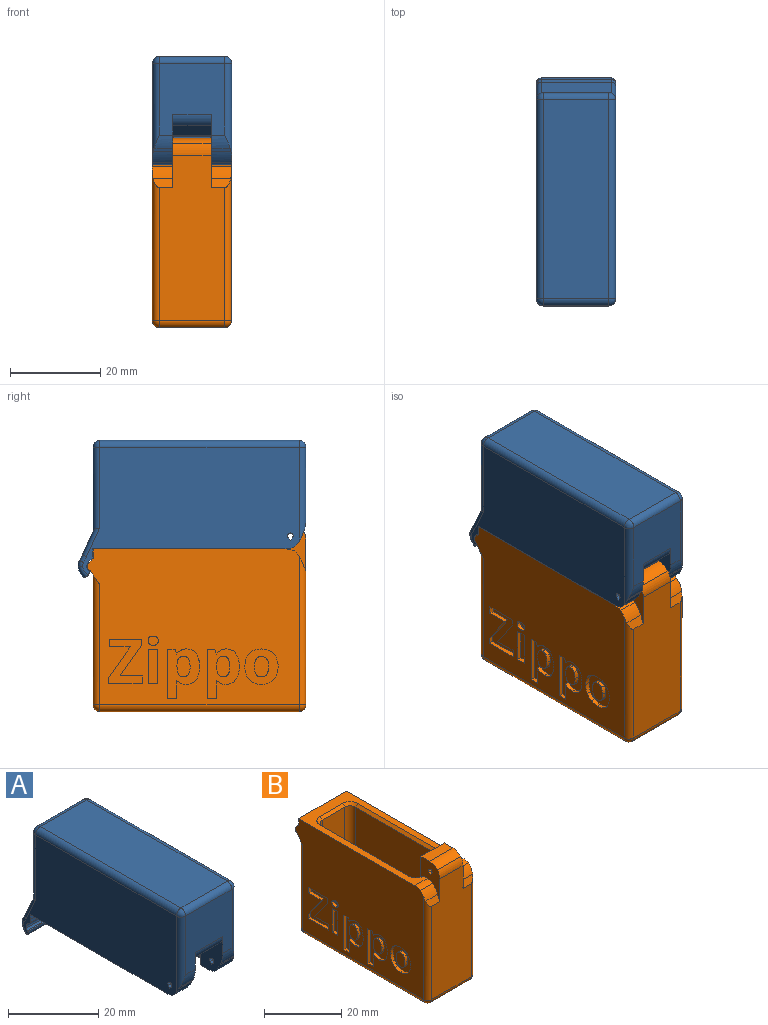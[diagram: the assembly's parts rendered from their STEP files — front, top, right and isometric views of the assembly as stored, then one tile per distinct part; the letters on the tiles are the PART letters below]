
ASSEMBLY  parts=2 mates=1
PART A: 71 faces, bbox 17.6x50.8x31 mm
  f0: plane 18.7x14.5mm, normal (0,1,0), area 271.2mm2, adj f27,f44,f45,f61
  f1: plane 15.91x14.5mm, normal (0,-1,0), area 191.4mm2, adj f15,f16,f50,f51,f54,f57,f58,f64
  f2: cylinder r=2mm len=21mm, axis (0,0,-1), area 64.4mm2, adj f3,f7,f12,f13,f15,f67
  f3: plane 13.1x8.2mm, normal (0,1,0), area 107.4mm2, adj f2,f4,f13,f66
  f4: cylinder r=2mm len=21mm, axis (0,0,-1), area 64.4mm2, adj f3,f8,f12,f13,f16,f65
  f5: plane 47.92x28.3mm, normal (-1,0,0), area 1000.2mm2, adj f12,f17,f18,f19,f24,f28,f29,f30
  f6: cylinder r=2mm len=21mm, axis (0,0,-1), area 66mm2, adj f7,f10,f12,f13
  f7: plane 32.2x21mm, normal (-1,0,0), area 676.2mm2, adj f2,f6,f12,f13
  f8: plane 32.2x21mm, normal (1,0,0), area 676.2mm2, adj f4,f9,f12,f13
  f9: cylinder r=2mm len=21mm, axis (0,0,-1), area 66mm2, adj f8,f10,f12,f13
  f10: plane 21x8.2mm, normal (0,-1,0), area 172.2mm2, adj f6,f9,f12,f13
  f11: plane 47.92x28.3mm, normal (1,0,0), area 1000.2mm2, adj f12,f20,f21,f22,f24,f28,f29,f30
  f12: plane 42.56x17.5mm, normal (0,0,-1), area 287.2mm2, adj f2,f4,f5,f6,f7,f8,f9,f10
  f13: plane 36.2x12.2mm, normal (0,0,-1), area 438.2mm2, adj f2,f3,f4,f6,f7,f8,f9,f10
  f14: plane 44.1x14.5mm, normal (0,0,1), area 639.4mm2, adj f56,f58,f61,f62
  f15: plane 11.19x6.94mm, normal (-1,0,0), area 45.1mm2, adj f1,f2,f12,f20,f21,f22,f23,f46
  f16: plane 11.19x6.94mm, normal (1,0,0), area 45.1mm2, adj f1,f4,f12,f17,f18,f19,f23,f47
  f17: plane 4.45x0.61mm, normal (0,0.79,0.61), area 3.4mm2, adj f5,f16,f18,f19
  f18: plane 4.45x0.61mm, normal (0,-0.79,0.61), area 3.4mm2, adj f5,f16,f17,f19
  f19: cylinder r=0.62mm len=4.45mm, axis (-1,0,0), area 12.7mm2, adj f5,f16,f17,f18
  f20: cylinder r=0.62mm len=4.45mm, axis (-1,0,0), area 12.7mm2, adj f11,f15,f21,f22
  f21: plane 4.45x0.61mm, normal (0,-0.79,0.61), area 3.4mm2, adj f11,f15,f20,f22
  f22: plane 4.45x0.61mm, normal (0,0.79,0.61), area 3.4mm2, adj f11,f15,f20,f21
  f23: plane 8.6x3.23mm, normal (0,-0.57,-0.82), area 33.9mm2, adj f15,f16,f64,f68,f69,f70
  f24: cylinder r=1.26mm len=17.5mm, axis (1,0,0), area 36.3mm2, adj f5,f11,f25,f34,f36,f40
  f25: cylinder r=3.7mm len=15.5mm, axis (1,0,0), area 43.2mm2, adj f24,f26,f36,f40
  f26: cylinder r=2.41mm len=15.5mm, axis (1,0,0), area 21.6mm2, adj f25,f35,f37,f41
  f27: plane 15.59x5.41mm, normal (0,0.91,0.42), area 87.7mm2, adj f0,f35,f39,f43,f44,f45
  f28: plane 17.5x1.21mm, normal (0,-1,0), area 21.2mm2, adj f5,f11,f12,f29
  f29: plane 17.5x0.87mm, normal (0,-1,0), area 15.1mm2, adj f5,f11,f28,f30
  f30: plane 17.5x0.36mm, normal (0,-0.69,-0.72), area 8.6mm2, adj f5,f11,f29,f31
  f31: cylinder r=4.29mm len=17.5mm, axis (1,0,0), area 17.6mm2, adj f5,f11,f30,f32
  f32: cylinder r=1.22mm len=17.5mm, axis (1,0,0), area 19.9mm2, adj f5,f11,f31,f33
  f33: cylinder r=1.4mm len=17.5mm, axis (1,0,0), area 11.3mm2, adj f5,f11,f32,f34
  f34: cylinder r=1.26mm len=17.5mm, axis (1,0,0), area 3.8mm2, adj f5,f11,f24,f33
  f35: cylinder r=15mm len=15.5mm, axis (1,0,0), area 21.5mm2, adj f26,f27,f38,f42
  f36: torus R=2.7mm, axis (1,0,0), area 4.3mm2, adj f11,f24,f25,f37
  f37: torus R=1.41mm, axis (1,0,0), area 1.9mm2, adj f11,f26,f36,f38
  f38: torus R=16mm, axis (1,0,0), area 2.2mm2, adj f11,f35,f37,f39
  f39: cylinder r=1mm len=6.84mm, axis (0,-0.42,0.91), area 10.1mm2, adj f11,f27,f38,f45
  f40: torus R=2.7mm, axis (1,0,0), area 4.3mm2, adj f5,f24,f25,f41
  f41: torus R=1.41mm, axis (1,0,0), area 1.9mm2, adj f5,f26,f40,f42
  f42: torus R=16mm, axis (1,0,0), area 2.2mm2, adj f5,f35,f41,f43
  f43: cylinder r=1mm len=6.84mm, axis (0,0.42,-0.91), area 10.1mm2, adj f5,f27,f42,f44
  f44: cylinder r=1.5mm len=18.7mm, axis (0,0,-1), area 43mm2, adj f0,f5,f27,f43,f59
  f45: cylinder r=1.5mm len=18.7mm, axis (0,0,1), area 43mm2, adj f0,f11,f27,f39,f63
  f46: plane 4.29x0.49mm, normal (0,-0.92,-0.38), area 2.2mm2, adj f15,f49,f50,f57
  f47: plane 4.29x0.49mm, normal (0,-0.92,-0.38), area 2.2mm2, adj f16,f48,f51,f54
  f48: cylinder r=8mm len=4.45mm, axis (1,0,0), area 13.9mm2, adj f5,f16,f47,f53,f54
  f49: cylinder r=8mm len=4.45mm, axis (1,0,0), area 13.9mm2, adj f11,f15,f46,f52,f57
  f50: cylinder r=8mm len=4.16mm, axis (-1,0,0), area 11.2mm2, adj f1,f15,f46,f57
  f51: cylinder r=8mm len=4.16mm, axis (-1,0,0), area 11.2mm2, adj f1,f16,f47,f54
  f52: cylinder r=5mm len=4.45mm, axis (1,0,0), area 9.6mm2, adj f11,f12,f15,f49
  f53: cylinder r=5mm len=4.45mm, axis (1,0,0), area 9.6mm2, adj f5,f12,f16,f48
  f54: cylinder r=1.5mm len=20.76mm, axis (0,0,1), area 43.4mm2, adj f1,f5,f47,f48,f51,f55
  f55: sphere r=1.5mm, area 3.5mm2, adj f54,f56,f58
  f56: cylinder r=1.5mm len=44.1mm, axis (0,1,0), area 103.9mm2, adj f5,f14,f55,f59
  f57: cylinder r=1.5mm len=20.76mm, axis (0,0,-1), area 43.4mm2, adj f1,f11,f46,f49,f50,f60
  f58: cylinder r=1.5mm len=14.5mm, axis (-1,0,0), area 34.2mm2, adj f1,f14,f55,f60
  f59: sphere r=1.5mm, area 4.8mm2, adj f44,f56,f61
  f60: sphere r=1.5mm, area 3.5mm2, adj f57,f58,f62
  f61: cylinder r=1.5mm len=14.5mm, axis (1,0,0), area 34.2mm2, adj f0,f14,f59,f63
  f62: cylinder r=1.5mm len=44.1mm, axis (0,-1,0), area 103.9mm2, adj f11,f14,f60,f63
  f63: sphere r=1.5mm, area 2.3mm2, adj f45,f61,f62
  f64: cylinder r=3mm len=8.6mm, axis (-1,0,0), area 24.8mm2, adj f1,f15,f16,f23
  f65: cone r=2mm half-angle=45deg, axis (0,0,-1), area 0.4mm2, adj f4,f16,f66,f70
  f66: plane 8.2x1.37mm, normal (0,0.71,-0.71), area 15.9mm2, adj f3,f65,f67,f69
  f67: cone r=2mm half-angle=45deg, axis (0,0,-1), area 0.4mm2, adj f2,f15,f66,f68
  f68: bspline ~1.03x0.24mm, area 0.2mm2, adj f15,f23,f67,f69
  f69: cylinder r=0.8mm len=8.2mm, axis (1,0,0), area 9.2mm2, adj f23,f66,f68,f70
  f70: bspline ~1.03x0.24mm, area 0.2mm2, adj f16,f23,f65,f69
PART B: 227 faces, bbox 17.5x48.4x41.9 mm
  f0: plane 44.1x14.5mm, normal (0,0,-1), area 594.4mm2, adj f125,f126,f127,f128,f129,f130,f131,f132
  f1: plane 46.9x34.5mm, normal (-1,0,0), area 1314.9mm2, adj f13,f14,f22,f23,f24,f25,f33,f34
  f2: plane 28.73x14.5mm, normal (0,1,0), area 416.5mm2, adj f25,f213,f214,f222
  f3: plane 36.65x14.5mm, normal (0,-1,0), area 488.5mm2, adj f16,f17,f207,f208,f211,f212,f218,f223
  f4: plane 46.9x34.5mm, normal (1,0,0), area 1533.1mm2, adj f13,f14,f22,f23,f24,f25,f210,f212
  f5: cylinder r=2mm len=32.2mm, axis (0,0,-1), area 101.2mm2, adj f6,f12,f15,f202
  f6: plane 32.2x32.2mm, normal (-1,0,0), area 1036.8mm2, adj f5,f7,f15,f201
  f7: cylinder r=2mm len=32.2mm, axis (0,0,-1), area 101.2mm2, adj f6,f8,f15,f200
  f8: plane 38.9x8.5mm, normal (0,1,0), area 321mm2, adj f7,f9,f15,f16,f17,f18,f200,f206
  f9: cylinder r=2mm len=32.2mm, axis (0,0,-1), area 101.2mm2, adj f8,f10,f15,f206
  f10: plane 32.2x32.2mm, normal (1,0,0), area 1036.8mm2, adj f9,f11,f15,f205
  f11: cylinder r=2mm len=32.2mm, axis (0,0,-1), area 101.2mm2, adj f10,f12,f15,f204
  f12: plane 32.2x8.2mm, normal (0,-1,0), area 264mm2, adj f5,f11,f15,f203
  f13: plane 17.5x2.1mm, normal (0,1,0), area 36.8mm2, adj f1,f4,f14,f22
  f14: plane 42.46x17.5mm, normal (0,0,1), area 215.8mm2, adj f1,f4,f13,f16,f17,f200,f201,f202
  f15: plane 36.2x12.2mm, normal (0,0,1), area 438.2mm2, adj f5,f6,f7,f8,f9,f10,f11,f12
  f16: plane 10.91x6.91mm, normal (-1,0,0), area 43.2mm2, adj f3,f8,f14,f18,f19,f20,f21,f206
  f17: plane 10.91x6.91mm, normal (1,0,0), area 43.2mm2, adj f3,f8,f14,f18,f19,f20,f21,f200
  f18: plane 8.5x3.16mm, normal (0,0,1), area 26.9mm2, adj f8,f16,f17,f217
  f19: cylinder r=0.62mm len=8.5mm, axis (-1,0,0), area 24.3mm2, adj f16,f17,f20,f21
  f20: plane 8.5x0.61mm, normal (0,-0.79,0.61), area 6.6mm2, adj f16,f17,f19,f21
  f21: plane 8.5x0.61mm, normal (0,0.79,0.61), area 6.6mm2, adj f16,f17,f19,f20
  f22: plane 17.5x0.81mm, normal (0,0.71,0.71), area 20.2mm2, adj f1,f4,f13,f23
  f23: cylinder r=2mm len=17.5mm, axis (-1,0,0), area 12mm2, adj f1,f4,f22,f24
  f24: cylinder r=1mm len=17.5mm, axis (-1,0,0), area 29mm2, adj f1,f4,f23,f25
  f25: plane 17.5x3.09mm, normal (0,0.82,-0.57), area 21.7mm2, adj f1,f2,f4,f24,f213,f214
  f26: extruded ~1.12x1mm, area 1.3mm2, adj f27,f48,f49,f116
  f27: extruded ~1.07x1mm, area 1.3mm2, adj f26,f28,f49,f116
  f28: extruded ~1.68x1mm, area 1.7mm2, adj f27,f29,f49,f116
  f29: extruded ~2.29x1.39mm, area 3mm2, adj f28,f30,f49,f116
  f30: extruded ~1.15x1mm, area 1.3mm2, adj f29,f31,f49,f116
  f31: extruded ~1.75x1mm, area 1.8mm2, adj f30,f32,f49,f116
  f32: plane 1x0.23mm, normal (0,1,0), area 0.2mm2, adj f31,f48,f49,f116
  f33: extruded ~2.09x1mm, area 2.4mm2, adj f1,f34,f47,f49
  f34: extruded ~1.54x1mm, area 1.6mm2, adj f1,f33,f35,f49
  f35: extruded ~1.36x1.01mm, area 1.7mm2, adj f1,f34,f36,f49
  f36: extruded ~2.11x1mm, area 2.1mm2, adj f1,f35,f37,f49
  f37: extruded ~2.88x1mm, area 3mm2, adj f1,f36,f38,f49
  f38: extruded ~2.1x1.04mm, area 2.4mm2, adj f1,f37,f39,f49
  f39: extruded ~2.15x1.12mm, area 2.5mm2, adj f1,f38,f40,f49
  f40: plane 1x0.1mm, normal (0,0,-1), area 0.1mm2, adj f1,f39,f41,f49
  f41: plane 1x0.98mm, normal (0,0.96,-0.28), area 1mm2, adj f1,f40,f42,f49
  f42: plane 1.68x1mm, normal (0,0,-1), area 1.7mm2, adj f1,f41,f43,f49
  f43: plane 10.91x1mm, normal (0,-1,0), area 10.9mm2, adj f1,f42,f44,f49
  f44: plane 2.07x1mm, normal (0,0,1), area 2.1mm2, adj f1,f43,f45,f49
  f45: plane 3.07x1mm, normal (0,1,0), area 3.1mm2, adj f1,f44,f46,f49
  f46: extruded ~1.1x1mm, area 1.1mm2, adj f1,f45,f47,f49
  f47: plane 1x0.11mm, normal (0,0,1), area 0.1mm2, adj f1,f33,f46,f49
  f48: extruded ~1.55x1mm, area 1.6mm2, adj f26,f32,f49,f116
  f49: plane 11.05x7.07mm, normal (-1,0,0), area 45.1mm2, adj f26,f27,f28,f29,f30,f31,f32,f33
  f50: extruded ~1.12x1mm, area 1.3mm2, adj f51,f72,f73,f117
  f51: extruded ~1.07x1mm, area 1.3mm2, adj f50,f52,f73,f117
  f52: extruded ~1.68x1mm, area 1.7mm2, adj f51,f53,f73,f117
  f53: extruded ~2.29x1.39mm, area 3mm2, adj f52,f54,f73,f117
  f54: extruded ~1.15x1mm, area 1.3mm2, adj f53,f55,f73,f117
  f55: extruded ~1.75x1mm, area 1.8mm2, adj f54,f56,f73,f117
  f56: plane 1x0.23mm, normal (0,1,0), area 0.2mm2, adj f55,f72,f73,f117
  f57: extruded ~2.09x1mm, area 2.4mm2, adj f1,f58,f71,f73
  f58: extruded ~1.54x1mm, area 1.6mm2, adj f1,f57,f59,f73
  f59: extruded ~1.36x1.01mm, area 1.7mm2, adj f1,f58,f60,f73
  f60: extruded ~2.11x1mm, area 2.1mm2, adj f1,f59,f61,f73
  f61: extruded ~2.88x1mm, area 3mm2, adj f1,f60,f62,f73
  f62: extruded ~2.1x1.04mm, area 2.4mm2, adj f1,f61,f63,f73
  f63: extruded ~2.15x1.12mm, area 2.5mm2, adj f1,f62,f64,f73
  f64: plane 1x0.1mm, normal (0,0,-1), area 0.1mm2, adj f1,f63,f65,f73
  f65: plane 1x0.98mm, normal (0,0.96,-0.28), area 1mm2, adj f1,f64,f66,f73
  f66: plane 1.68x1mm, normal (0,0,-1), area 1.7mm2, adj f1,f65,f67,f73
  f67: plane 10.91x1mm, normal (0,-1,0), area 10.9mm2, adj f1,f66,f68,f73
  f68: plane 2.07x1mm, normal (0,0,1), area 2.1mm2, adj f1,f67,f69,f73
  f69: plane 3.07x1mm, normal (0,1,0), area 3.1mm2, adj f1,f68,f70,f73
  f70: extruded ~1.1x1mm, area 1.1mm2, adj f1,f69,f71,f73
  f71: plane 1x0.11mm, normal (0,0,1), area 0.1mm2, adj f1,f57,f70,f73
  f72: extruded ~1.55x1mm, area 1.6mm2, adj f50,f56,f73,f117
  f73: plane 11.05x7.07mm, normal (-1,0,0), area 45.1mm2, adj f50,f51,f52,f53,f54,f55,f56,f57
  f74: extruded ~2.89x1mm, area 3.1mm2, adj f1,f75,f91,f92
  f75: extruded ~2.08x1mm, area 2.1mm2, adj f1,f74,f76,f92
  f76: extruded ~1.36x1.28mm, area 1.9mm2, adj f1,f75,f77,f92
  f77: extruded ~1.92x1mm, area 2mm2, adj f1,f76,f78,f92
  f78: extruded ~2.72x1.03mm, area 3mm2, adj f1,f77,f79,f92
  f79: extruded ~2.89x1mm, area 3.1mm2, adj f1,f78,f80,f92
  f80: extruded ~2.09x1mm, area 2.2mm2, adj f1,f79,f81,f92
  f81: extruded ~1.37x1.28mm, area 1.9mm2, adj f1,f80,f82,f92
  f82: extruded ~1.92x1mm, area 2mm2, adj f1,f81,f91,f92
  f83: extruded ~1.7x1mm, area 1.8mm2, adj f84,f90,f92,f93
  f84: extruded ~1.69x1mm, area 1.8mm2, adj f83,f85,f92,f93
  f85: extruded ~1.19x1mm, area 1.4mm2, adj f84,f86,f92,f93
  f86: extruded ~1.2x1mm, area 1.4mm2, adj f85,f87,f92,f93
  f87: extruded ~1.69x1mm, area 1.7mm2, adj f86,f88,f92,f93
  f88: extruded ~1.7x1mm, area 1.8mm2, adj f87,f89,f92,f93
  f89: extruded ~1.19x1mm, area 1.4mm2, adj f88,f90,f92,f93
  f90: extruded ~1.2x1mm, area 1.4mm2, adj f83,f89,f92,f93
  f91: extruded ~2.72x1.04mm, area 3mm2, adj f1,f74,f82,f92
  f92: plane 7.85x7.34mm, normal (-1,0,0), area 35.1mm2, adj f74,f75,f76,f77,f78,f79,f80,f81
  f93: plane 4.53x3.12mm, normal (-1,0,0), area 11.9mm2, adj f83,f84,f85,f86,f87,f88,f89,f90
  f94: plane 2.07x1mm, normal (0,0,1), area 2.1mm2, adj f1,f95,f97,f98
  f95: plane 7.58x1mm, normal (0,1,0), area 7.6mm2, adj f1,f94,f96,f98
  f96: plane 2.07x1mm, normal (0,0,-1), area 2.1mm2, adj f1,f95,f97,f98
  f97: plane 7.58x1mm, normal (0,-1,0), area 7.6mm2, adj f1,f94,f96,f98
  f98: plane 7.58x2.07mm, normal (-1,0,0), area 15.7mm2, adj f94,f95,f96,f97
  f99: extruded ~1.13x1.01mm, area 1.7mm2, adj f1,f100,f103,f104
  f100: extruded ~1.13x1.02mm, area 1.7mm2, adj f1,f99,f101,f104
  f101: extruded ~1x0.84mm, area 0.9mm2, adj f1,f100,f102,f104
  f102: extruded ~1x0.75mm, area 0.8mm2, adj f1,f101,f103,f104
  f103: extruded ~1.13x1.01mm, area 1.7mm2, adj f1,f99,f102,f104
  f104: plane 2.25x2.03mm, normal (-1,0,0), area 3.8mm2, adj f99,f100,f101,f102,f103
  f105: plane 7.37x1mm, normal (0,0,1), area 7.4mm2, adj f1,f106,f114,f115
  f106: plane 1.73x1mm, normal (0,1,0), area 1.7mm2, adj f1,f105,f107,f115
  f107: plane 4.87x1mm, normal (0,0,-1), area 4.9mm2, adj f1,f106,f108,f115
  f108: plane 6.82x4.74mm, normal (0,0.82,0.57), area 8.3mm2, adj f1,f107,f109,f115
  f109: plane 1.36x1mm, normal (0,1,0), area 1.4mm2, adj f1,f108,f110,f115
  f110: plane 7.11x1mm, normal (0,0,-1), area 7.1mm2, adj f1,f109,f111,f115
  f111: plane 1.73x1mm, normal (0,-1,0), area 1.7mm2, adj f1,f110,f112,f115
  f112: plane 4.62x1mm, normal (0,0,1), area 4.6mm2, adj f1,f111,f113,f115
  f113: plane 6.81x4.75mm, normal (0,-0.82,-0.57), area 8.3mm2, adj f1,f112,f114,f115
  f114: plane 1.36x1mm, normal (0,-1,0), area 1.4mm2, adj f1,f105,f113,f115
  f115: plane 9.91x7.37mm, normal (-1,0,0), area 39.4mm2, adj f105,f106,f107,f108,f109,f110,f111,f112
  f116: plane 4.53x2.9mm, normal (-1,0,0), area 11.1mm2, adj f26,f27,f28,f29,f30,f31,f32,f48
  f117: plane 4.53x2.9mm, normal (-1,0,0), area 11.1mm2, adj f50,f51,f52,f53,f54,f55,f56,f72
  f118: extruded ~0.52x0.4mm, area 0.2mm2, adj f119,f143,f144,f198
  f119: extruded ~0.56x0.4mm, area 0.3mm2, adj f118,f120,f144,f198
  f120: extruded ~0.7x0.4mm, area 0.3mm2, adj f119,f121,f144,f198
  f121: extruded ~0.49x0.4mm, area 0.2mm2, adj f120,f122,f144,f198
  f122: extruded ~0.56x0.4mm, area 0.2mm2, adj f121,f123,f144,f198
  f123: extruded ~0.52x0.4mm, area 0.2mm2, adj f122,f124,f144,f198
  f124: extruded ~0.59x0.4mm, area 0.2mm2, adj f123,f143,f144,f198
  f125: extruded ~2.25x0.63mm, area 1mm2, adj f0,f126,f142,f144
  f126: extruded ~1.2x0.4mm, area 0.5mm2, adj f0,f125,f127,f144
  f127: extruded ~0.77x0.65mm, area 0.4mm2, adj f0,f126,f128,f144
  f128: extruded ~0.99x0.4mm, area 0.4mm2, adj f0,f127,f129,f144
  f129: extruded ~1.27x0.48mm, area 0.6mm2, adj f0,f128,f130,f144
  f130: extruded ~1.29x0.47mm, area 0.6mm2, adj f0,f129,f131,f144
  f131: extruded ~1.19x0.4mm, area 0.5mm2, adj f0,f130,f132,f144
  f132: extruded ~1.05x0.43mm, area 0.5mm2, adj f0,f131,f133,f144
  f133: extruded ~0.66x0.4mm, area 0.3mm2, adj f0,f132,f134,f144
  f134: extruded ~0.47x0.46mm, area 0.3mm2, adj f0,f133,f135,f144
  f135: plane 0.4x0.04mm, normal (-1,0,0), area 0mm2, adj f0,f134,f136,f144
  f136: extruded ~0.94x0.4mm, area 0.4mm2, adj f0,f135,f137,f144
  f137: extruded ~0.53x0.5mm, area 0.3mm2, adj f0,f136,f138,f144
  f138: extruded ~0.89x0.4mm, area 0.4mm2, adj f0,f137,f139,f144
  f139: extruded ~0.61x0.4mm, area 0.2mm2, adj f0,f138,f140,f144
  f140: plane 0.86x0.4mm, normal (0,-1,0), area 0.3mm2, adj f0,f139,f141,f144
  f141: extruded ~0.69x0.4mm, area 0.3mm2, adj f0,f140,f142,f144
  f142: extruded ~1.92x0.74mm, area 0.9mm2, adj f0,f125,f141,f144
  f143: extruded ~0.66x0.4mm, area 0.3mm2, adj f118,f124,f144,f198
  f144: plane 5.22x3.59mm, normal (0,0,-1), area 11.1mm2, adj f118,f119,f120,f121,f122,f123,f124,f125
  f145: extruded ~1.34x0.4mm, area 0.5mm2, adj f146,f160,f161,f199
  f146: extruded ~1.35x0.4mm, area 0.5mm2, adj f145,f147,f161,f199
  f147: extruded ~0.54x0.41mm, area 0.3mm2, adj f146,f148,f161,f199
  f148: extruded ~0.54x0.41mm, area 0.3mm2, adj f147,f149,f161,f199
  f149: extruded ~1.35x0.4mm, area 0.5mm2, adj f148,f150,f161,f199
  f150: extruded ~1.34x0.4mm, area 0.5mm2, adj f149,f151,f161,f199
  f151: extruded ~0.54x0.41mm, area 0.3mm2, adj f150,f160,f161,f199
  f152: extruded ~1.97x0.44mm, area 0.8mm2, adj f0,f153,f159,f161
  f153: extruded ~1.96x0.45mm, area 0.8mm2, adj f0,f152,f154,f161
  f154: extruded ~1.33x0.67mm, area 0.6mm2, adj f0,f153,f155,f161
  f155: extruded ~1.34x0.64mm, area 0.6mm2, adj f0,f154,f156,f161
  f156: extruded ~1.99x0.44mm, area 0.8mm2, adj f0,f155,f157,f161
  f157: extruded ~1.95x0.45mm, area 0.8mm2, adj f0,f156,f158,f161
  f158: extruded ~1.33x0.66mm, area 0.6mm2, adj f0,f157,f159,f161
  f159: extruded ~1.35x0.64mm, area 0.6mm2, adj f0,f152,f158,f161
  f160: extruded ~0.55x0.41mm, area 0.3mm2, adj f145,f151,f161,f199
  f161: plane 5.24x3.56mm, normal (0,0,-1), area 11.4mm2, adj f145,f146,f147,f148,f149,f150,f151,f152
  f162: plane 1.08x0.4mm, normal (-1,0,0), area 0.4mm2, adj f0,f163,f171,f172
  f163: plane 5.09x0.4mm, normal (0,1,0), area 2mm2, adj f0,f162,f164,f172
  f164: plane 0.89x0.4mm, normal (1,0,0), area 0.4mm2, adj f0,f163,f165,f172
  f165: plane 1.64x1.31mm, normal (0.78,-0.62,0), area 0.8mm2, adj f0,f164,f166,f172
  f166: plane 0.65x0.52mm, normal (-0.63,-0.78,0), area 0.3mm2, adj f0,f165,f167,f172
  f167: plane 0.59x0.47mm, normal (-0.78,0.63,0), area 0.3mm2, adj f0,f166,f168,f172
  f168: extruded ~0.4x0.37mm, area 0.2mm2, adj f0,f167,f169,f172
  f169: plane 0.53x0.4mm, normal (0.03,-1,0), area 0.2mm2, adj f0,f168,f170,f172
  f170: plane 0.48x0.4mm, normal (0.02,-1,0), area 0.2mm2, adj f0,f169,f171,f172
  f171: plane 2.95x0.4mm, normal (0,-1,0), area 1.2mm2, adj f0,f162,f170,f172
  f172: plane 5.09x2.53mm, normal (0,0,-1), area 6.7mm2, adj f162,f163,f164,f165,f166,f167,f168,f169
  f173: plane 3.56x0.4mm, normal (-1,0,0), area 1.4mm2, adj f0,f174,f196,f197
  f174: plane 0.91x0.4mm, normal (0,1,0), area 0.4mm2, adj f0,f173,f175,f197
  f175: plane 2.22x0.4mm, normal (1,0,0), area 0.9mm2, adj f0,f174,f176,f197
  f176: plane 0.4x0.05mm, normal (0,1,0), area 0mm2, adj f0,f175,f177,f197
  f177: plane 0.66x0.62mm, normal (-0.73,0.69,0), area 0.4mm2, adj f0,f176,f178,f197
  f178: extruded ~0.92x0.91mm, area 0.5mm2, adj f0,f177,f179,f197
  f179: extruded ~0.63x0.4mm, area 0.3mm2, adj f0,f178,f180,f197
  f180: extruded ~0.66x0.4mm, area 0.3mm2, adj f0,f179,f181,f197
  f181: extruded ~0.72x0.4mm, area 0.3mm2, adj f0,f180,f182,f197
  f182: extruded ~0.57x0.49mm, area 0.3mm2, adj f0,f181,f183,f197
  f183: extruded ~0.84x0.4mm, area 0.3mm2, adj f0,f182,f184,f197
  f184: extruded ~0.65x0.4mm, area 0.3mm2, adj f0,f183,f185,f197
  f185: extruded ~0.54x0.4mm, area 0.2mm2, adj f0,f184,f186,f197
  f186: extruded ~0.62x0.45mm, area 0.3mm2, adj f0,f185,f187,f197
  f187: plane 0.69x0.59mm, normal (-0.65,-0.76,0), area 0.4mm2, adj f0,f186,f188,f197
  f188: extruded ~0.58x0.4mm, area 0.3mm2, adj f0,f187,f189,f197
  f189: extruded ~0.57x0.4mm, area 0.2mm2, adj f0,f188,f190,f197
  f190: extruded ~0.45x0.4mm, area 0.2mm2, adj f0,f189,f191,f197
  f191: extruded ~0.46x0.4mm, area 0.2mm2, adj f0,f190,f192,f197
  f192: extruded ~0.4x0.4mm, area 0.2mm2, adj f0,f191,f193,f197
  f193: extruded ~0.42x0.4mm, area 0.2mm2, adj f0,f192,f194,f197
  f194: extruded ~0.81x0.74mm, area 0.4mm2, adj f0,f193,f195,f197
  f195: plane 1.29x1.28mm, normal (0.7,-0.71,0), area 0.7mm2, adj f0,f194,f196,f197
  f196: plane 0.75x0.4mm, normal (0,-1,0), area 0.3mm2, adj f0,f173,f195,f197
  f197: plane 5.16x3.57mm, normal (0,0,-1), area 9.7mm2, adj f173,f174,f175,f176,f177,f178,f179,f180
  f198: plane 1.69x1.48mm, normal (0,0,-1), area 2mm2, adj f118,f119,f120,f121,f122,f123,f124,f143
  f199: plane 3.5x1.42mm, normal (0,0,-1), area 4.2mm2, adj f145,f146,f147,f148,f149,f150,f151,f160
  f200: cone r=2mm half-angle=45deg, axis (0,0,1), area 4.1mm2, adj f7,f8,f14,f17,f201
  f201: plane 32.2x0.8mm, normal (-0.71,0,0.71), area 36.4mm2, adj f6,f14,f200,f202
  f202: cone r=2mm half-angle=45deg, axis (0,0,1), area 4.3mm2, adj f5,f14,f201,f203
  f203: plane 8.2x0.8mm, normal (0,-0.71,0.71), area 9.3mm2, adj f12,f14,f202,f204
  f204: cone r=2mm half-angle=45deg, axis (0,0,1), area 4.3mm2, adj f11,f14,f203,f205
  f205: plane 32.2x0.8mm, normal (0.71,0,0.71), area 36.4mm2, adj f10,f14,f204,f206
  f206: cone r=2mm half-angle=45deg, axis (0,0,1), area 4.1mm2, adj f8,f9,f14,f16,f205
  f207: plane 4.33x1.94mm, normal (0,-0.92,0.38), area 8.3mm2, adj f3,f17,f210,f212
  f208: plane 4.33x1.94mm, normal (0,-0.92,0.38), area 8.3mm2, adj f3,f16,f209,f211
  f209: cylinder r=8mm len=4.5mm, axis (-1,0,0), area 14mm2, adj f1,f16,f208,f211,f216
  f210: cylinder r=8mm len=4.5mm, axis (-1,0,0), area 14mm2, adj f4,f17,f207,f212,f215
  f211: cylinder r=1.5mm len=32.76mm, axis (0,0,1), area 72.5mm2, adj f1,f3,f208,f209,f221
  f212: cylinder r=1.5mm len=32.76mm, axis (0,0,-1), area 72.5mm2, adj f3,f4,f207,f210,f225
  f213: cylinder r=1.5mm len=28.73mm, axis (0,0,-1), area 65.8mm2, adj f1,f2,f25,f220
  f214: cylinder r=1.5mm len=28.73mm, axis (0,0,1), area 65.8mm2, adj f2,f4,f25,f224
  f215: cylinder r=5mm len=4.5mm, axis (1,0,0), area 9.7mm2, adj f4,f14,f17,f210
  f216: cylinder r=5mm len=4.5mm, axis (1,0,0), area 9.7mm2, adj f1,f14,f16,f209
  f217: cylinder r=4.2mm len=8.5mm, axis (-1,0,0), area 28mm2, adj f16,f17,f18,f218
  f218: cylinder r=4.5mm len=8.5mm, axis (1,0,0), area 22.7mm2, adj f3,f16,f17,f217
  f219: cylinder r=1.5mm len=44.1mm, axis (0,1,0), area 103.9mm2, adj f0,f1,f220,f221
  f220: sphere r=1.5mm, area 3.5mm2, adj f213,f219,f222
  f221: sphere r=1.5mm, area 3.5mm2, adj f211,f219,f223
  f222: cylinder r=1.5mm len=14.5mm, axis (1,0,0), area 34.2mm2, adj f0,f2,f220,f224
  f223: cylinder r=1.5mm len=14.5mm, axis (-1,0,0), area 34.2mm2, adj f0,f3,f221,f225
  f224: sphere r=1.5mm, area 3.5mm2, adj f214,f222,f226
  f225: sphere r=1.5mm, area 3.5mm2, adj f212,f223,f226
  f226: cylinder r=1.5mm len=44.1mm, axis (0,-1,0), area 103.9mm2, adj f0,f4,f224,f225
PLACE A t=(-16.7,-5.34,-10.68)mm
PLACE B t=(-16.75,-5.34,-10.68)mm
MATE revolute A.f19 <-> B.f19  axis (1,0,0) through (-21,-26.88,25.22)mm
